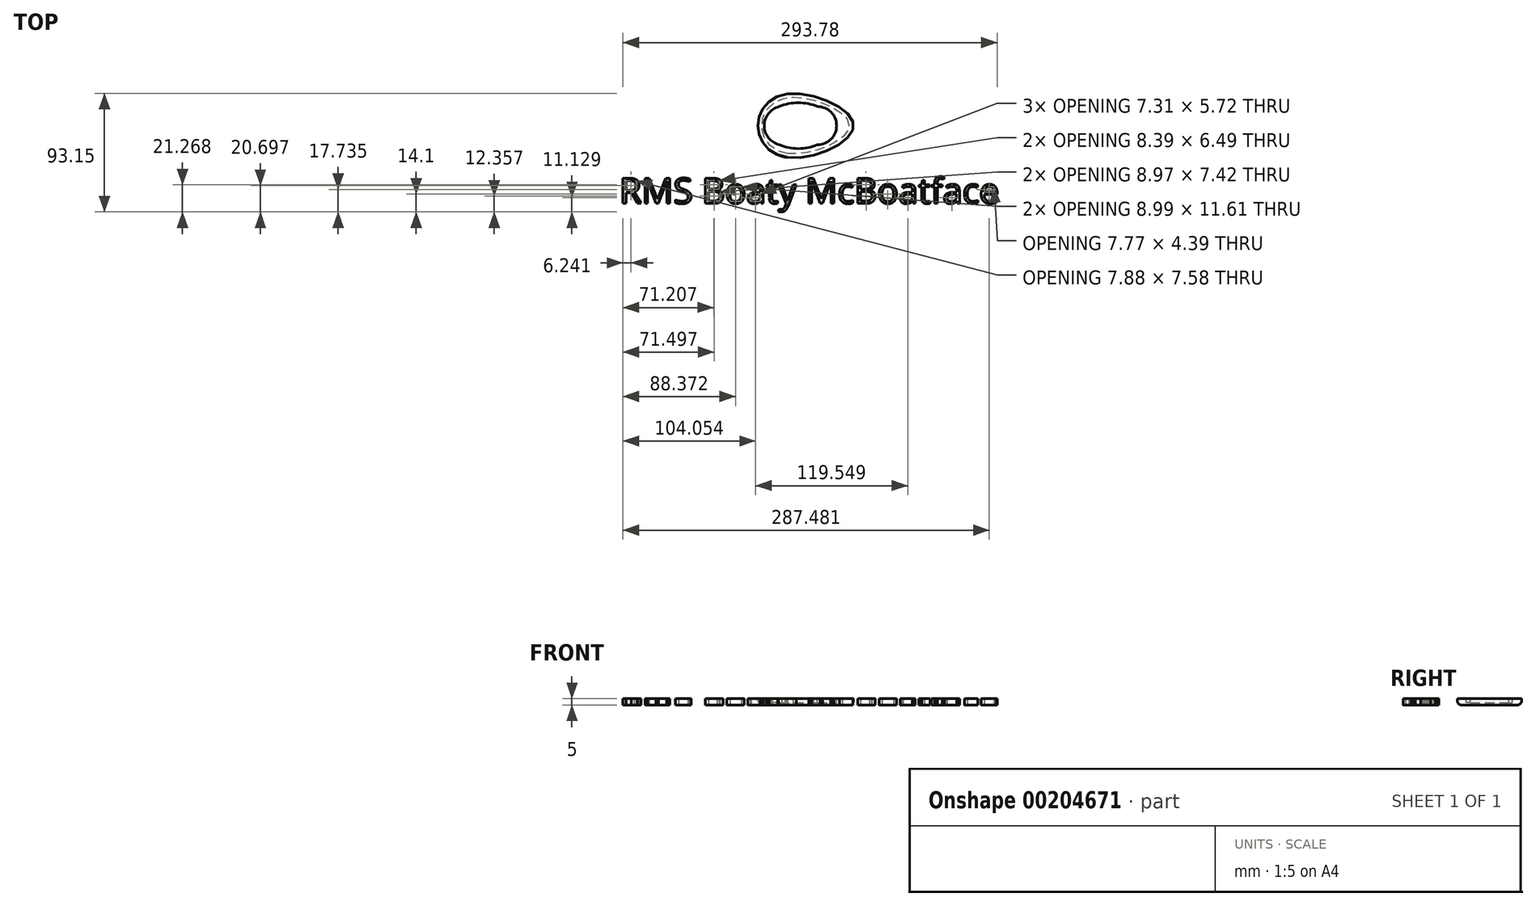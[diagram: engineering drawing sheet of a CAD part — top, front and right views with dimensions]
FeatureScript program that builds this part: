
annotation { "Feature Type Name" : "Feature", "Feature Type Description" : "" }
export const myFeature = defineFeature(function(context is Context, id is Id, definition is map)
    precondition{}
    {
        {
            var Q0;
            Q0=qCreatedBy(makeId("Top.planeOp"),FACE);
            var sketch = newSketch(context, id + "F0", { "sketchPlane" : qUnion([Q0])});
            skPoint(sketch, "E0.middle", {"position": v(0, 0) * mm});
            skFitSpline(sketch, "E1", {"points": [v(-17.06, -25) * mm, v(-40.24, 0) * mm, v(-17.06, 25) * mm, v(34.76, 0) * mm, v(-17.06, -25) * mm]});
            skSolve(sketch);
        }
        {
            var Q0;
            Q0 = qSketchRegion(id + "F0", true);
            extrude(context, id + "F1", {"entities" : qUnion([Q0]), "depth" : 5 * mm});
        }
        {
            var Q0;
            Q0=makeQuery(id+"F1.opExtrude","CAP_EDGE",EDGE,{"disambiguationData":[OSD([sQuery(id+"F0.wireOp",EDGE,"E1")])],"isStart":true});
            fillet(context, id + "F2", {"entities" : qUnion([Q0]), "radius" : 3 * mm, "tangentPropagation" : true, "rho" : 0.3, "crossSection" : FilletCrossSection.CONIC, "allowEdgeOverflow" : false});
        }
        {
            var Q0;
            Q0=makeQuery(id+"F1.opExtrude","CAP_FACE",FACE,{"disambiguationData":[OSD([sQuery(id+"F0.wireOp",EDGE,"E1")])],"isStart":false});
            var sketch = newSketch(context, id + "F3", { "sketchPlane" : qUnion([Q0])});
            skLineSegment(sketch, "E2.bottom", {"start": v(-23.5, -15) * mm, "end": v(6.5, -15) * mm});
            skLineSegment(sketch, "E2.top", {"start": v(-23.5, 15) * mm, "end": v(6.5, 15) * mm});
            skLineSegment(sketch, "E2.left", {"start": v(-23.5, -15) * mm, "end": v(-23.5, 15) * mm});
            skLineSegment(sketch, "E2.right", {"start": v(6.5, -15) * mm, "end": v(6.5, 15) * mm});
            skPoint(sketch, "E3", {"position": v(0, 0) * mm});
            skArc(sketch, "E4", {"start": v(6.5, -15) * mm, "mid": v(21.5, 0) * mm, "end": v(6.5, 15) * mm});
            skArc(sketch, "E5", {"start": v(-23.5, 15) * mm, "mid": v(-35.32, 0) * mm, "end": v(-23.5, -15) * mm});
            skArc(sketch, "E6", {"start": v(6.5, 15) * mm, "mid": v(-8.5, 17.93) * mm, "end": v(-23.5, 15) * mm});
            skArc(sketch, "E7", {"start": v(-23.5, -15) * mm, "mid": v(-8.5, -18.1) * mm, "end": v(6.5, -15) * mm});
            skSolve(sketch);
        }
        {
            var Q0;
            Q0 = qSketchRegion(id + "F3", true);
            extrude(context, id + "F4", {"entities" : qUnion([Q0]), "operationType" : NewBodyOperationType.REMOVE, "oppositeDirection" : true, "depth" : 3 * mm});
        }
        {
            var Q0;
            Q0=qCreatedBy(makeId("Top.planeOp"),FACE);
            var sketch = newSketch(context, id + "F5", { "sketchPlane" : qUnion([Q0])});
            skText(sketch, "E8", { "text": "RMS Boaty McBoatface", "fontName": "OpenSans-Regular.ttf"});
            const initialGuessF5  = {"E8": [-0.14893, -0.06117, 1, 0, 0.02]};
            skSetInitialGuess(sketch, initialGuessF5);
            skSolve(sketch);
        }
        {
            var Q0;
            Q0 = qSketchRegion(id + "F5", true);
            extrude(context, id + "F6", {"entities" : qUnion([Q0]), "depth" : 5 * mm});
        }
    });
